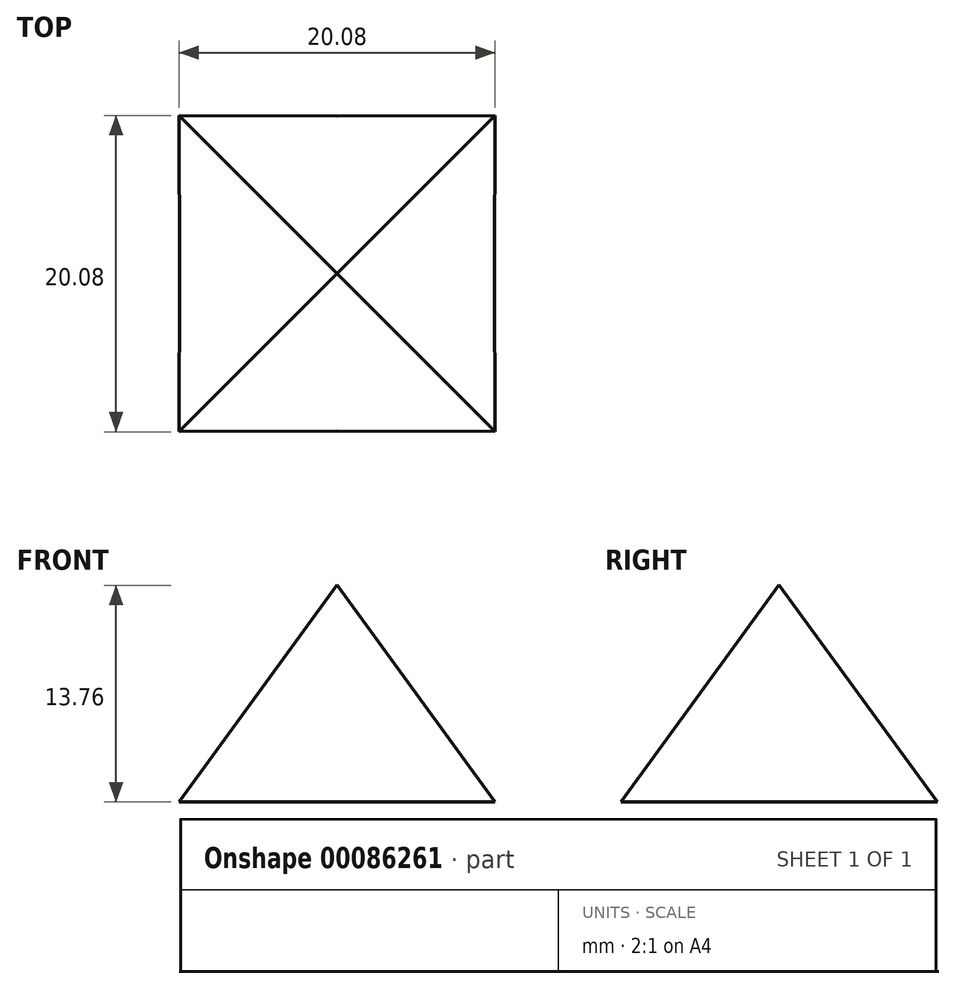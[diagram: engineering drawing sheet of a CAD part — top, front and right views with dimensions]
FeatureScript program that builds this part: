
annotation { "Feature Type Name" : "Feature", "Feature Type Description" : "" }
export const myFeature = defineFeature(function(context is Context, id is Id, definition is map)
    precondition{}
    {
        {
            var Q0;
            Q0=qCreatedBy(makeId("Front.planeOp"),FACE);
            var sketch = newSketch(context, id + "F0", { "sketchPlane" : qUnion([Q0])});
            skLineSegment(sketch, "E0", {"start": v(0, 0) * mm, "end": v(0, -3.3) * mm, "construction": true});
            skLineSegment(sketch, "E1", {"start": v(0, 0) * mm, "end": v(0, 13.76) * mm, "construction": true});
            skLineSegment(sketch, "E2", {"start": v(0, 13.76) * mm, "end": v(-10, 0) * mm});
            skLineSegment(sketch, "E3", {"start": v(-10, 0) * mm, "end": v(0, 0) * mm});
            skLineSegment(sketch, "E4.MirrorCS", {"start": v(0, 13.76) * mm, "end": v(10, 0) * mm});
            skLineSegment(sketch, "E5.MirrorCS", {"start": v(10, 0) * mm, "end": v(0, 0) * mm});
            skPoint(sketch, "E6", {"position": v(0, 13.76) * mm});
            skLineSegment(sketch, "E7", {"start": v(39.12, 30.16) * mm, "end": v(-2.96, 52.53) * mm});
            skLineSegment(sketch, "E8", {"start": v(-2.96, 52.53) * mm, "end": v(-2.96, 42.74) * mm});
            skLineSegment(sketch, "E9", {"start": v(-2.96, 42.74) * mm, "end": v(39.12, 20.36) * mm});
            skLineSegment(sketch, "E10", {"start": v(39.12, 20.36) * mm, "end": v(39.12, 30.16) * mm});
            skSolve(sketch);
        }
        {
            var Q0;
            Q0=qCreatedBy(makeId("Top.planeOp"),FACE);
            var sketch = newSketch(context, id + "F1", { "sketchPlane" : qUnion([Q0])});
            skLineSegment(sketch, "E11.0", {"start": v(-10, 0) * mm, "end": v(0, 0) * mm, "construction": true});
            skLineSegment(sketch, "E12", {"start": v(-10, 0) * mm, "end": v(-10.04, 10.04) * mm});
            skLineSegment(sketch, "E13", {"start": v(0, 0) * mm, "end": v(0, 10) * mm, "construction": true});
            skLineSegment(sketch, "E14", {"start": v(-10, 0) * mm, "end": v(-10, 10) * mm, "construction": true});
            skLineSegment(sketch, "E15", {"start": v(-10, 10) * mm, "end": v(-10.04, 10.04) * mm, "construction": true});
            skLineSegment(sketch, "E16.MirrorCS", {"start": v(10, 0) * mm, "end": v(10.04, 10.04) * mm});
            skLineSegment(sketch, "E17.MirrorCS", {"start": v(-10, 0) * mm, "end": v(-10.04, -10.04) * mm});
            skLineSegment(sketch, "E18.MirrorCS", {"start": v(10, 0) * mm, "end": v(10.04, -10.04) * mm});
            skLineSegment(sketch, "E19.MirrorCS", {"start": v(0, 10) * mm, "end": v(-10.04, 10.04) * mm});
            skLineSegment(sketch, "E20.MirrorCS", {"start": v(0, -10) * mm, "end": v(-10.04, -10.04) * mm});
            skLineSegment(sketch, "E21.MirrorCS", {"start": v(0, -10) * mm, "end": v(10.04, -10.04) * mm});
            skLineSegment(sketch, "E22.MirrorCS", {"start": v(0, 10) * mm, "end": v(10.04, 10.04) * mm});
            skSolve(sketch);
        }
        {
            var Q0;
            Q0=makeQuery(id+"F1.imprint","IMPRINT",FACE,{"disambiguationData":[TD([[makeQuery(id+"F1.imprint","IMPRINT",EDGE,{"derivedFrom":sQuery(id+"F1.wireOp",EDGE,"E12")}),-1.0]])]});
            var Q1;
            Q1=sQuery(id+"F0.wireOp",VERTEX,"E6");
            loft(context, id + "F2", {"sheetProfilesArray" : [{ "sheetProfileEntities" : qUnion([Q0]) }, { "sheetProfileEntities" : qUnion([Q1]) }]});
        }
    });
